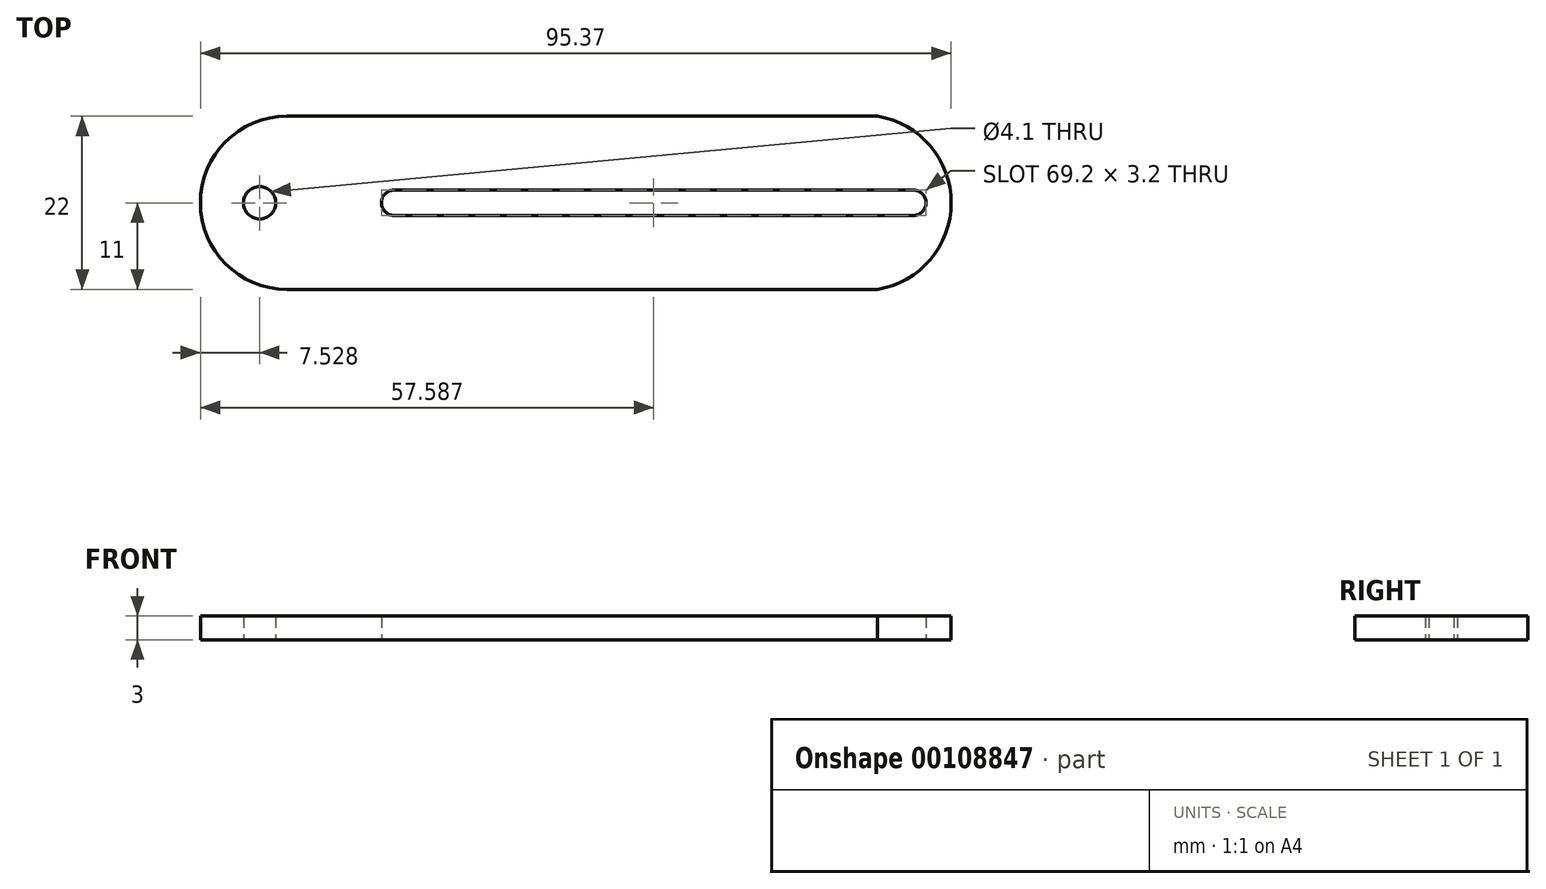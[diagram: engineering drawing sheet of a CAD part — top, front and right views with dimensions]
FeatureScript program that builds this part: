
annotation { "Feature Type Name" : "Feature", "Feature Type Description" : "" }
export const myFeature = defineFeature(function(context is Context, id is Id, definition is map)
    precondition{}
    {
        {
            var Q0;
            Q0=qCreatedBy(makeId("Top.planeOp"),FACE);
            var sketch = newSketch(context, id + "F0", { "sketchPlane" : qUnion([Q0])});
            skLineSegment(sketch, "E0", {"start": v(-67.36, 0) * mm, "end": v(60.86, 0) * mm, "construction": true});
            skLineSegment(sketch, "E1", {"start": v(0, 50.5) * mm, "end": v(0, -35.66) * mm, "construction": true});
            skLineSegment(sketch, "E2", {"start": v(-61.97, 11) * mm, "end": v(13.03, 11) * mm});
            skLineSegment(sketch, "E3.MirrorCS", {"start": v(-61.97, -11) * mm, "end": v(13.03, -11) * mm});
            skArc(sketch, "E4", {"start": v(-61.97, 11) * mm, "mid": v(-72.97, 0) * mm, "end": v(-61.97, -11) * mm});
            skArc(sketch, "E5", {"start": v(13.03, -11) * mm, "mid": v(22.4, 0) * mm, "end": v(13.03, 11) * mm});
            skLineSegment(sketch, "E6", {"start": v(-65.44, 6.64) * mm, "end": v(-65.44, -6.23) * mm, "construction": true});
            skPoint(sketch, "E7", {"position": v(-65.44, 0) * mm});
            skLineSegment(sketch, "E8", {"start": v(-48.38, 1.6) * mm, "end": v(17.62, 1.6) * mm});
            skLineSegment(sketch, "E9.MirrorCS", {"start": v(-48.38, -1.6) * mm, "end": v(17.62, -1.6) * mm});
            skArc(sketch, "E10", {"start": v(17.62, -1.6) * mm, "mid": v(19.22, 0) * mm, "end": v(17.62, 1.6) * mm});
            skArc(sketch, "E11", {"start": v(-48.38, 1.6) * mm, "mid": v(-49.98, 0) * mm, "end": v(-48.38, -1.6) * mm});
            skSolve(sketch);
        }
        {
            var Q0;
            Q0=makeQuery(id+"F0.imprint","IMPRINT",FACE,{"disambiguationData":[TD([[makeQuery(id+"F0.imprint","IMPRINT",EDGE,{"derivedFrom":sQuery(id+"F0.wireOp",EDGE,"E2")}),-1.0]])]});
            extrude(context, id + "F1", {"entities" : qUnion([Q0]), "depth" : 3 * mm});
        }
        {
            var Q0;
            Q0=sQuery(id+"F0.wireOp",VERTEX,"E7");
            var Q1;
            Q1=makeQuery(id+"F1.opExtrude","SWEPT_BODY",BODY,{"disambiguationData":[OSD([sQuery(id+"F0.wireOp",EDGE,"E2"),sQuery(id+"F0.wireOp",EDGE,"E3.MirrorCS"),sQuery(id+"F0.wireOp",EDGE,"E4"),sQuery(id+"F0.wireOp",EDGE,"E5"),sQuery(id+"F0.wireOp",EDGE,"E8"),sQuery(id+"F0.wireOp",EDGE,"E9.MirrorCS"),sQuery(id+"F0.wireOp",EDGE,"E10"),sQuery(id+"F0.wireOp",EDGE,"E11")])]});
            hole(context, id + "F2", {"style" : HoleStyle.SIMPLE, "endStyle" : HoleEndStyle.THROUGH, "oppositeDirection" : true, "standardTappedOrClearance" : lookupTablePath({ "standard" : "ISO", "engagement" : "75%", "pitch" : "0.9 mm", "size" : "M5", "type" : "Tapped" }), "standardBlindInLast" : lookupTablePath({ "standard" : "ISO", "engagement" : "75%", "pitch" : "0.9 mm", "size" : "M5", "type" : "Tapped" }), "holeDiameter" : 4.1 * mm, "startFromSketch" : true, "locations" : qUnion([Q0]), "scope" : qUnion([Q1]), "isTappedThrough" : true, "showTappedDepth" : true});
        }
    });
